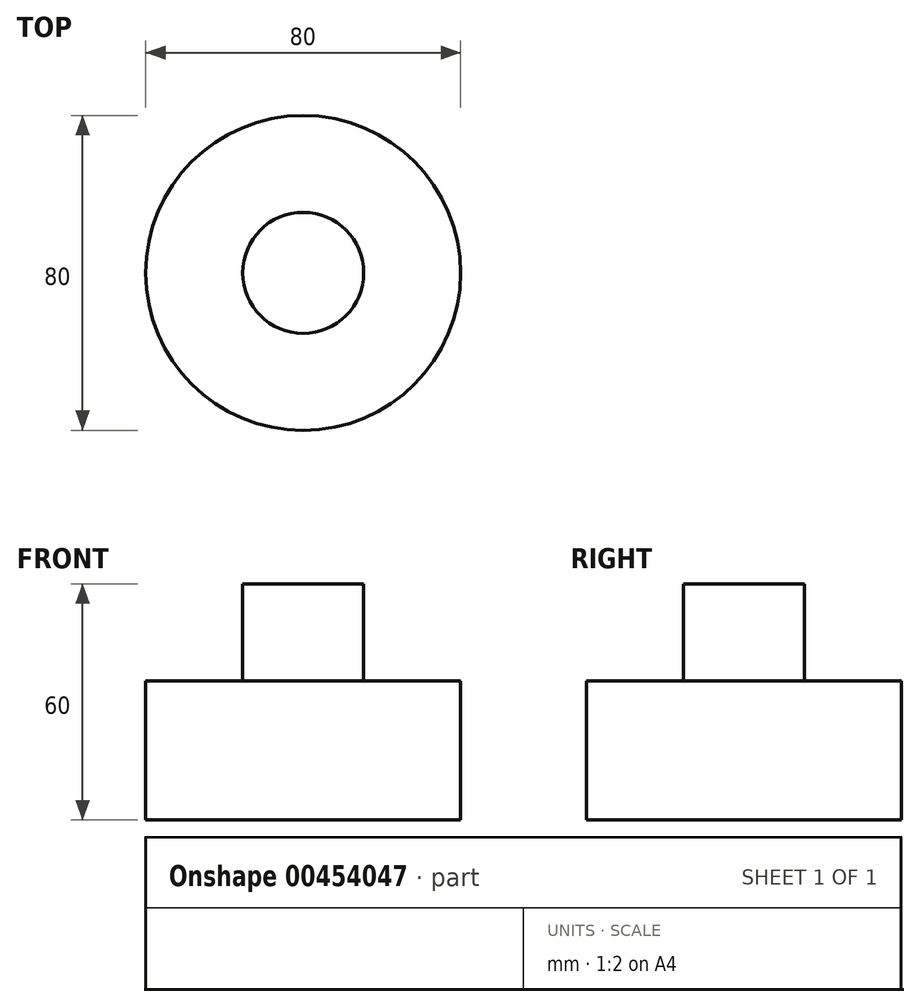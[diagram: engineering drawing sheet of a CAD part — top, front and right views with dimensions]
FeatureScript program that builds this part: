
annotation { "Feature Type Name" : "Feature", "Feature Type Description" : "" }
export const myFeature = defineFeature(function(context is Context, id is Id, definition is map)
    precondition{}
    {
        {
            var Q0;
            Q0=qCreatedBy(makeId("Front.planeOp"),FACE);
            var sketch = newSketch(context, id + "F0", { "sketchPlane" : qUnion([Q0])});
            skLineSegment(sketch, "E0.bottom", {"start": v(0, 0) * mm, "end": v(-40, 0) * mm});
            skLineSegment(sketch, "E0.top", {"start": v(0, 60) * mm, "end": v(-40, 60) * mm});
            skLineSegment(sketch, "E0.left", {"start": v(0, 0) * mm, "end": v(0, 60) * mm});
            skLineSegment(sketch, "E0.right", {"start": v(-40, 0) * mm, "end": v(-40, 60) * mm});
            skSolve(sketch);
        }
        {
            var Q0;
            Q0=makeQuery(id+"F0.imprint","IMPRINT",FACE,{"disambiguationData":[TD([[makeQuery(id+"F0.imprint","IMPRINT",EDGE,{"derivedFrom":sQuery(id+"F0.wireOp",EDGE,"E0.bottom")}),-1.0]])]});
            var Q1;
            Q1=sQuery(id+"F0.wireOp",EDGE,"E0.left");
            revolve(context, id + "F1", {"entities" : qUnion([Q0]), "axis" : qUnion([Q1]), "revolveType" : RevolveType.FULL});
        }
        {
            var Q0;
            Q0=qCreatedBy(makeId("Front.planeOp"),FACE);
            var sketch = newSketch(context, id + "F2", { "sketchPlane" : qUnion([Q0])});
            skLineSegment(sketch, "E1", {"start": v(0, 61.92) * mm, "end": v(0, 34.83) * mm});
            skLineSegment(sketch, "E2.bottom", {"start": v(-47.31, 60.47) * mm, "end": v(-15.38, 60.47) * mm});
            skLineSegment(sketch, "E2.top", {"start": v(-47.31, 35.32) * mm, "end": v(-15.38, 35.32) * mm});
            skLineSegment(sketch, "E2.left", {"start": v(-47.31, 60.47) * mm, "end": v(-47.31, 35.32) * mm});
            skLineSegment(sketch, "E2.right", {"start": v(-15.38, 60.47) * mm, "end": v(-15.38, 35.32) * mm});
            skSolve(sketch);
        }
        {
            var Q0;
            Q0 = qSketchRegion(id + "F2", true);
            var Q1;
            Q1=sQuery(id+"F2.wireOp",EDGE,"E1");
            revolve(context, id + "F3", {"operationType" : NewBodyOperationType.REMOVE, "entities" : qUnion([Q0]), "axis" : qUnion([Q1]), "revolveType" : RevolveType.FULL, "oppositeDirection" : true});
        }
    });
